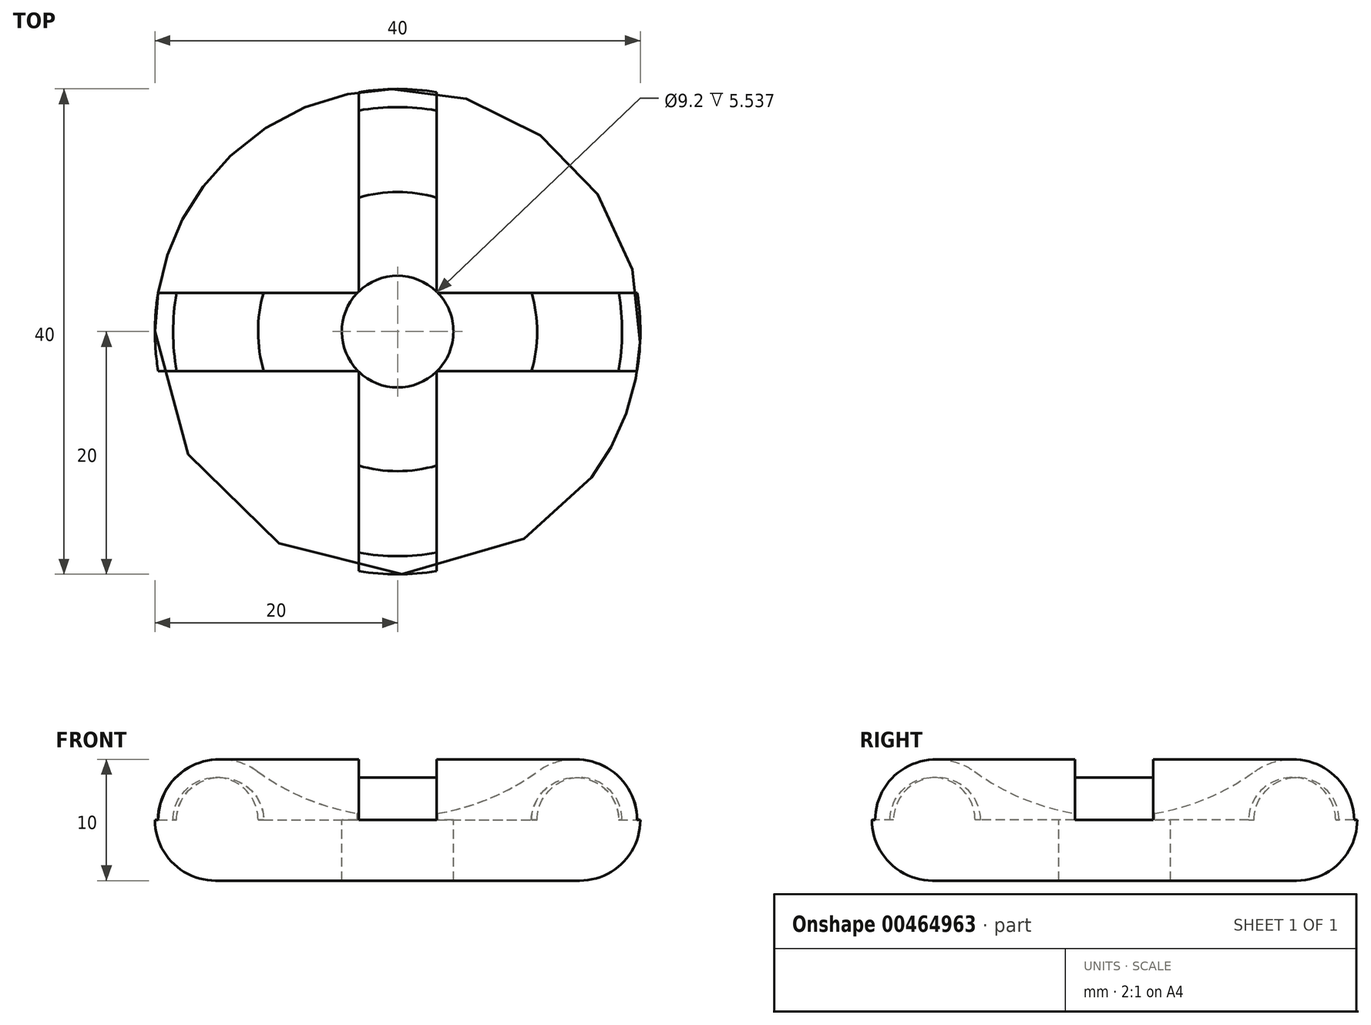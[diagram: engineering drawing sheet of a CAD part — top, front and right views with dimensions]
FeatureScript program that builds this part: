
annotation { "Feature Type Name" : "Feature", "Feature Type Description" : "" }
export const myFeature = defineFeature(function(context is Context, id is Id, definition is map)
    precondition{}
    {
        {
            var Q0;
            Q0=qCreatedBy(makeId("Front.planeOp"),FACE);
            var sketch = newSketch(context, id + "F0", { "sketchPlane" : qUnion([Q0])});
            skArc(sketch, "E0", {"start": v(-12, 9) * mm, "mid": v(-19.74, 6.58) * mm, "end": v(-15, 0) * mm});
            skLineSegment(sketch, "E1", {"start": v(-15, 0) * mm, "end": v(0, 0) * mm});
            skArc(sketch, "E2", {"start": v(-12, 9) * mm, "mid": v(-6.32, 6.03) * mm, "end": v(0, 5) * mm});
            skLineSegment(sketch, "E3", {"start": v(0, 0) * mm, "end": v(0, 5) * mm});
            skSolve(sketch);
        }
        {
            var Q0;
            Q0=makeQuery(id+"F0.imprint","IMPRINT",FACE,{"disambiguationData":[TD([[makeQuery(id+"F0.imprint","IMPRINT",EDGE,{"derivedFrom":sQuery(id+"F0.wireOp",EDGE,"E0")}),1.0]])]});
            var Q1;
            Q1=sQuery(id+"F0.wireOp",EDGE,"E3");
            revolve(context, id + "F1", {"entities" : qUnion([Q0]), "axis" : qUnion([Q1]), "revolveType" : RevolveType.FULL});
        }
        {
            var Q0;
            Q0=qCreatedBy(makeId("Top.planeOp"),FACE);
            cPlane(context, id + "F2", {"entities" : qUnion([Q0]), "cplaneType" : CPlaneType.OFFSET, "offset" : 10 * mm, "width" : 150 * mm, "height" : 150 * mm});
        }
        {
            var Q0;
            Q0=qCreatedBy(id+"F2.planeOp",FACE);
            var sketch = newSketch(context, id + "F3", { "sketchPlane" : qUnion([Q0])});
            skLineSegment(sketch, "E4.bottom", {"start": v(3.21, 21.14) * mm, "end": v(-3.21, 21.14) * mm});
            skLineSegment(sketch, "E4.top", {"start": v(3.21, -21.14) * mm, "end": v(-3.21, -21.14) * mm});
            skLineSegment(sketch, "E4.left", {"start": v(3.21, 21.14) * mm, "end": v(3.21, -21.14) * mm});
            skLineSegment(sketch, "E4.right", {"start": v(-3.21, 21.14) * mm, "end": v(-3.21, -21.14) * mm});
            skPoint(sketch, "E4.middle", {"position": v(0, 0) * mm});
            skLineSegment(sketch, "E5.bottom", {"start": v(-21.27, 3.18) * mm, "end": v(-21.27, -3.25) * mm});
            skLineSegment(sketch, "E5.top", {"start": v(21.01, 3.18) * mm, "end": v(21.01, -3.25) * mm});
            skLineSegment(sketch, "E5.left", {"start": v(-21.27, 3.18) * mm, "end": v(21.01, 3.18) * mm});
            skLineSegment(sketch, "E5.right", {"start": v(-21.27, -3.25) * mm, "end": v(21.01, -3.25) * mm});
            skPoint(sketch, "E5.middle", {"position": v(-0.13, -0.03) * mm});
            skSolve(sketch);
        }
        {
            var Q0;
            Q0 = qSketchRegion(id + "F3", true);
            extrude(context, id + "F4", {"entities" : qUnion([Q0]), "operationType" : NewBodyOperationType.REMOVE, "oppositeDirection" : true, "depth" : 5 * mm});
        }
        {
            var Q0;
            Q0=qCreatedBy(makeId("Front.planeOp"),FACE);
            var sketch = newSketch(context, id + "F5", { "sketchPlane" : qUnion([Q0])});
            skCircle(sketch, "E6", {"center": v(-15, 5) * mm, "radius": 3.5 * mm});
            skSolve(sketch);
        }
        {
            var Q0;
            Q0 = qSketchRegion(id + "F5", true);
            var Q1;
            Q1=sQuery(id+"F0.wireOp",EDGE,"E3");
            revolve(context, id + "F6", {"operationType" : NewBodyOperationType.ADD, "entities" : qUnion([Q0]), "axis" : qUnion([Q1]), "revolveType" : RevolveType.FULL});
        }
        {
            var Q0;
            Q0=qCreatedBy(id+"F2.planeOp",FACE);
            var sketch = newSketch(context, id + "F7", { "sketchPlane" : qUnion([Q0])});
            skCircle(sketch, "E7", {"center": v(0, 0) * mm, "radius": 4.6 * mm});
            skSolve(sketch);
        }
        {
            var Q0;
            Q0 = qSketchRegion(id + "F7", true);
            extrude(context, id + "F8", {"entities" : qUnion([Q0]), "operationType" : NewBodyOperationType.REMOVE, "oppositeDirection" : true, "depth" : 25 * mm});
        }
    });
